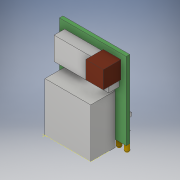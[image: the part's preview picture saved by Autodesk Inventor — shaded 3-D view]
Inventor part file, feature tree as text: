
AUTODESK INVENTOR PART (.ipt)
format: ipt  version: 2019 (Build 230136000, 136)  size: 334,848 bytes
history: native  units: mm
features: sketch x19, extrude x16, other x2, fillet x1
ambient origin geometry x8: Origin, YZ Plane, XZ Plane, XY Plane, X Axis, Y Axis, Z Axis, Center Point
bodies: Solid1 (feature_tree)
feature tree (38):
  extrude  "Extrusion1"  Depth=22.0mm
  extrude  "Extrusion2"  Depth=2.9mm
  extrude  "Extrusion3"  Depth=13.0mm
  extrude  "Extrusion4"  Depth=7.0mm TaperAngle=0.0deg
  extrude  "Extrusion5"  Depth=5.0mm
  extrude  "Extrusion6"  Depth=5.5mm
  extrude  "Extrusion7"  Depth=8.0mm
  extrude  "Extrusion8"  Depth=1.5mm
  extrude  "Extrusion9"  Depth=1.5mm
  extrude  "Extrusion10"  Depth=16.0mm
  extrude  "Extrusion11"  Depth=3.0mm TaperAngle=0.0deg
  sketch  "Sketch12"  dims[d26=5.0mm d27=5.0mm]
  extrude  "Extrusion12"  Depth=5.0mm
  extrude  "Extrusion13"  Depth=11.0mm
  extrude  "Extrusion14"  Depth=0.5mm TaperAngle=0.0deg
  extrude  "Extrusion15"  Depth=2.0mm
  extrude  "Extrusion16"  Depth=1.0mm
  fillet  "Fillet1"  Radius=6.0mm
  sketch  "Sketch18"  dims[d41=0.5mm]
  sketch  "Sketch19"  dims[d42=1.0mm d43=1.25mm d44=1.0mm d45=0.5mm d46=1.5mm d47=0.0mm d48=1.25mm d49=1.5mm d50=1.25mm d51=1.5mm d52=0.5mm d53=0.0mm d54=0.625mm d55=0.625mm d56=1.0mm d57=0.625mm d58=0.625mm d59=1.0mm d60=3.5mm d61=0.0mm d62=1.25mm d63=5.25mm d64=0.0mm d65=1.0mm d66=6.5mm d67=1.25mm d68=1.0mm d69=1.0mm d70=1.0mm d71=1.25mm d72=1.0mm d73=1.5mm d74=0.0mm d75=0.625mm d76=0.625mm d77=1.0mm d78=0.625mm d79=0.625mm d80=1.0mm d81=3.5mm d82=0.0mm d83=1.25mm d84=5.25mm d85=0.0mm d86=1.25mm d87=5.25mm d88=0.0mm d89=1.25mm d90=5.25mm d91=0.0mm d92=0.5mm]
  sketch  "Sketch1"  dims[d0=19.0mm d1=22.0mm]
  sketch  "Sketch2"  dims[d2=1.0mm d3=0.0mm d4=2.9mm]
  sketch  "Sketch3"  dims[d5=12.0mm d6=13.0mm]
  sketch  "Sketch4"  dims[d7=14.0mm d8=7.0mm d9=0.0mm]
  sketch  "Sketch5"  dims[d10=5.5mm d11=5.0mm]
  sketch  "Sketch6"  dims[d12=8.0mm d13=5.5mm]
  sketch  "Sketch7"  dims[d14=3.0mm d15=0.0mm d16=8.0mm]
  sketch  "Sketch8"  dims[d17=1.5mm d18=1.5mm]
  sketch  "Sketch9"  dims[d19=1.5mm d20=1.5mm]
  sketch  "Sketch10"  dims[d21=1.5mm d22=16.0mm]
  sketch  "Sketch11"  dims[d23=7.0mm d24=3.0mm d25=0.0mm]
  sketch  "Sketch13"  dims[d28=2.0mm d29=0.0mm d30=11.0mm]
  sketch  "Sketch14"  dims[d31=3.0mm d32=0.5mm d33=0.0mm]
  sketch  "Sketch15"  dims[d34=3.0mm d35=2.0mm]
  sketch  "Sketch16"  dims[d36=0.5mm d37=0.0mm d38=1.0mm d39=6.0mm]
  sketch  "Sketch17"  dims[d40=1.25mm]
  other  "Image1"
  other  "Image2"
